# Revit family: FOUR B-FRESH
name_source: partatom
category: Mechanical Equipment
units: mm (PartAtom-declared; Revit-internal decimal feet)

## family parameters
Always vertical = Yes
Cut with Voids When Loaded = No
OmniClass Number = 23.75.10.24.21.11.11
OmniClass Title = Packaged Refrigerant Condensing Coils and Fan Units
Part Type = Normal
Room Calculation Point = No
Round Connector Dimension = Use Radius
Shared = No
Work Plane-Based = No

## types (8) — shared parameters
Access Material = Metal Blue
B H/2 = 55 mm  [stored 0.180446 ft]
B H1 = 40 mm
Base Height = 100 mm  [stored 0.328084 ft]
Base Material = Metal Black
Body Material = Metal White
Description = AIR PRUFIER WITH OPTIONAL UV LAMB
Manufacturer = DOGU HVAC
Panel Thickness = 5 mm  [stored 0.0164042 ft]
URL = https://www.doguiklimlendirme.com
URL-TR = https://www.doguiklimlendirme.com
Voltage = 230 V

## per-type parameters (varying)
| type | Airflow (m3/h) | FILTER | H | L | Model | Panel H | Panel H/2 | Panel W | Power Cunsumption (Range) | Recommended Use Area(m2) | W | Weight (kg) | Writing H |
| K55.08.EC.0 | 160-800 | ISO Epm1+H14 Hepa | 1249 mm | 550 mm | B-FRESH-08-EC-WO.UVC | 23 mm | 11 mm | 28 mm | 38-220 | 21-120 | 657 mm | 60.00 kg | 937 mm |
| K55.20.EC.1 | 400-2000 | ISO Epm1+H14 Hepa+UVC | 1599 mm | 780 mm | B-FRESH-20-EC-W.UVC | 34 mm | 17 mm | 39 mm | 68-430 | 55-270 | 657 mm | 85.00 kg | 1199 mm |
| K55.12.EC.1 | 240-1200 | ISO Epm1+H14 Hepa+UVC | 1399 mm | 650 mm | B-FRESH-12-EC-W.UVC | 28 mm | 14 mm  [stored 0.0459318 ft] | 32 mm  [stored 0.104987 ft] | 45-275 | 32-200 | 657 mm | 80.00 kg | 1049 mm |
| K55.08.EC.1 | 160-800 | ISO Epm1+H14 Hepa+UVC | 1399 mm | 550 mm | B-FRESH-08-EC-W.UVC | 23 mm | 11 mm | 32 mm  [stored 0.104987 ft] | 38-220 | 21-120 | 657 mm | 70.00 kg | 1049 mm |
| K55.05.EC.1 | 110-550 | ISO Epm1+H14 Hepa+UVC | 1264 mm | 480 mm  [stored 1.5748 ft] | B-FRESH-05-EC-W.UVC | 19 mm  [stored 0.062336 ft] | 10 mm  [stored 0.0328084 ft] | 28 mm | 25-142 | 15-80 | 577 mm  [stored 1.89304 ft] | 65.00 kg | 948 mm |
| K55.20.EC.0 | 400-2000 | ISO Epm1+H14 Hepa | 1449 mm | 780 mm | B-FRESH-20-EC-WO.UVC | 34 mm | 17 mm | 34 mm | 68-430 | 55-270 | 657 mm | 75.00 kg | 1087 mm |
| K55.12.EC.0 | 240-1200 | ISO Epm1+H14 Hepa | 1249 mm | 650 mm | B-FRESH-12-EC-WO.UVC | 28 mm | 14 mm  [stored 0.0459318 ft] | 28 mm | 45-275 | 32-200 | 657 mm | 70.00 kg | 937 mm |
| K55.05.EC.0 | 110-550 | ISO Epm1+H14 Hepa | 1114 mm  [stored 3.65486 ft] | 480 mm  [stored 1.5748 ft] | B-FRESH-05-EC-WO.UVC | 19 mm  [stored 0.062336 ft] | 10 mm  [stored 0.0328084 ft] | 24 mm | 25-142 | 15-80 | 577 mm  [stored 1.89304 ft] | 55.00 kg | 836 mm |

note: column(s) folded — value = type name in every type: Product ID

note: [stored X ft] marks values corroborated as IEEE doubles in the binary element streams (Revit-internal decimal feet)

## geometry (parser evidence)
native form markers: Sweep x6
no freeform markers — native parametric forms only
